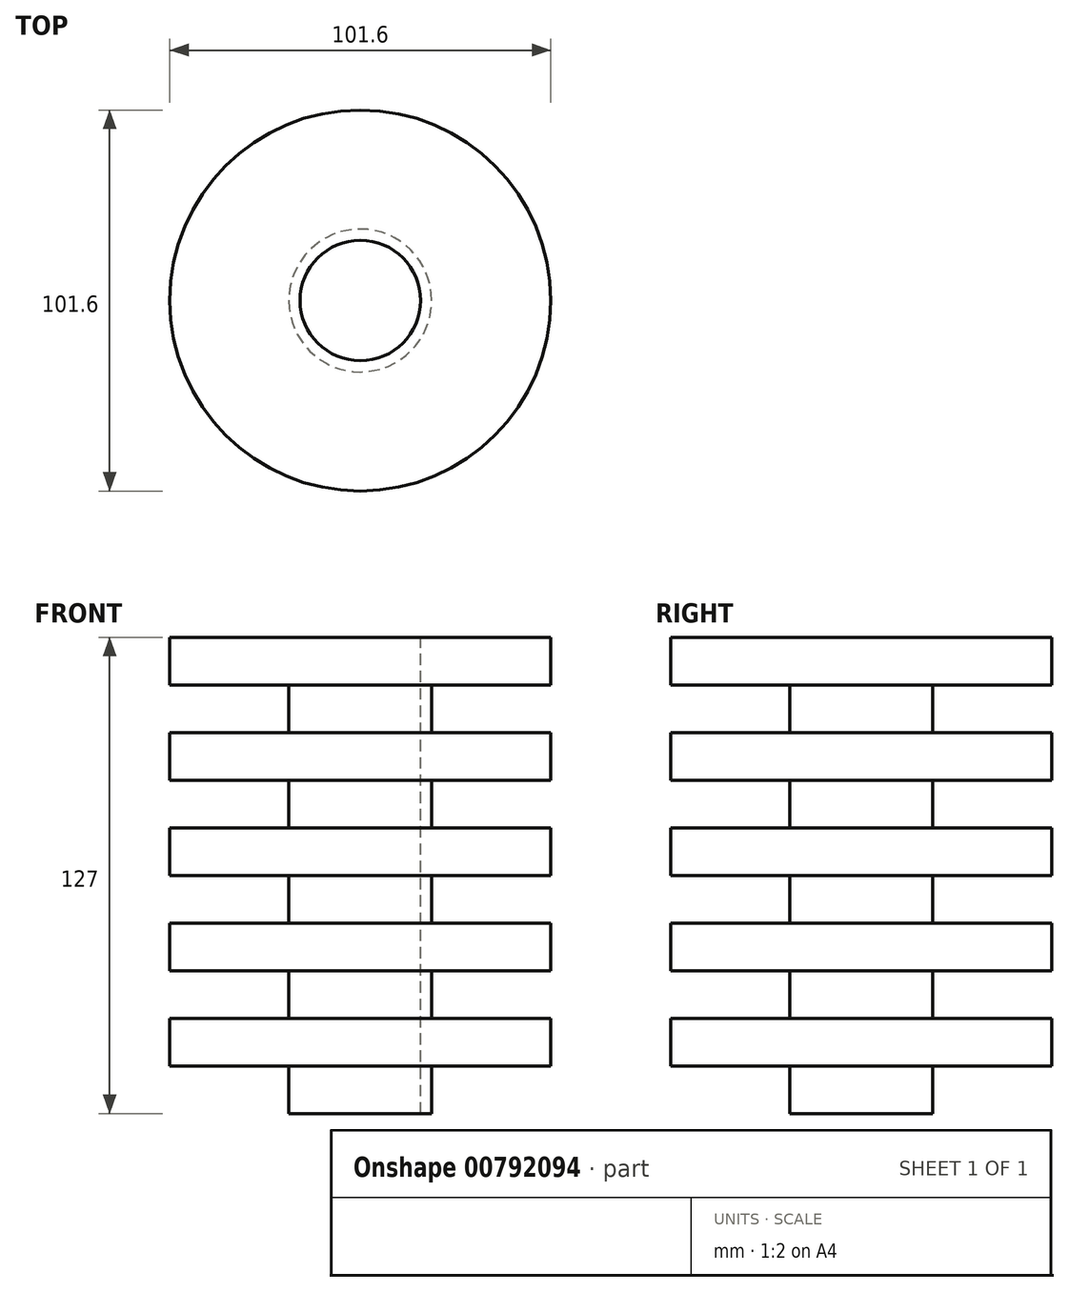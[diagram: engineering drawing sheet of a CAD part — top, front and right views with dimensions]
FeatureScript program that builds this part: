
annotation { "Feature Type Name" : "Feature", "Feature Type Description" : "" }
export const myFeature = defineFeature(function(context is Context, id is Id, definition is map)
    precondition{}
    {
        {
            var Q0;
            Q0=qCreatedBy(makeId("Front.planeOp"),FACE);
            var sketch = newSketch(context, id + "F0", { "sketchPlane" : qUnion([Q0])});
            skLineSegment(sketch, "E0", {"start": v(0, 0) * mm, "end": v(0, 127) * mm});
            skLineSegment(sketch, "E1", {"start": v(0, 127) * mm, "end": v(50.8, 127) * mm});
            skLineSegment(sketch, "E2", {"start": v(50.8, 127) * mm, "end": v(50.8, 114.3) * mm});
            skLineSegment(sketch, "E3", {"start": v(50.8, 114.3) * mm, "end": v(19.05, 114.3) * mm});
            skLineSegment(sketch, "E4", {"start": v(19.05, 114.3) * mm, "end": v(19.05, 101.6) * mm});
            skLineSegment(sketch, "E5", {"start": v(19.05, 101.6) * mm, "end": v(50.8, 101.6) * mm});
            skLineSegment(sketch, "E6", {"start": v(50.8, 101.6) * mm, "end": v(50.8, 88.9) * mm});
            skLineSegment(sketch, "E7", {"start": v(50.8, 88.9) * mm, "end": v(19.05, 88.9) * mm});
            skLineSegment(sketch, "E8", {"start": v(19.05, 88.9) * mm, "end": v(19.05, 76.2) * mm});
            skLineSegment(sketch, "E9", {"start": v(19.05, 76.2) * mm, "end": v(50.8, 76.2) * mm});
            skLineSegment(sketch, "E10", {"start": v(50.8, 76.2) * mm, "end": v(50.8, 63.5) * mm});
            skLineSegment(sketch, "E11", {"start": v(50.8, 63.5) * mm, "end": v(19.05, 63.5) * mm});
            skLineSegment(sketch, "E12", {"start": v(19.05, 63.5) * mm, "end": v(19.05, 50.8) * mm});
            skLineSegment(sketch, "E13", {"start": v(19.05, 50.8) * mm, "end": v(50.8, 50.8) * mm});
            skLineSegment(sketch, "E14", {"start": v(50.8, 50.8) * mm, "end": v(50.8, 38.1) * mm});
            skLineSegment(sketch, "E15", {"start": v(50.8, 38.1) * mm, "end": v(19.05, 38.1) * mm});
            skLineSegment(sketch, "E16", {"start": v(19.05, 38.1) * mm, "end": v(19.05, 25.4) * mm});
            skLineSegment(sketch, "E17", {"start": v(19.05, 25.4) * mm, "end": v(50.8, 25.4) * mm});
            skLineSegment(sketch, "E18", {"start": v(50.8, 25.4) * mm, "end": v(50.8, 12.7) * mm});
            skLineSegment(sketch, "E19", {"start": v(50.8, 12.7) * mm, "end": v(19.05, 12.7) * mm});
            skLineSegment(sketch, "E20", {"start": v(19.05, 12.7) * mm, "end": v(19.05, 0) * mm});
            skLineSegment(sketch, "E21", {"start": v(19.05, 0) * mm, "end": v(0, 0) * mm});
            skSolve(sketch);
        }
        {
            var Q0;
            Q0=makeQuery(id+"F0.imprint","IMPRINT",FACE,{"disambiguationData":[TD([[makeQuery(id+"F0.imprint","IMPRINT",EDGE,{"derivedFrom":sQuery(id+"F0.wireOp",EDGE,"E0")}),-1.0]])]});
            var Q1;
            Q1=sQuery(id+"F0.wireOp",EDGE,"E0");
            revolve(context, id + "F1", {"surfaceOperationType" : NewSurfaceOperationType.NEW, "entities" : qUnion([Q0]), "axis" : qUnion([Q1]), "revolveType" : RevolveType.FULL});
        }
        {
            var Q0;
            Q0=makeQuery(id+"F1.opRevolve","SWEPT_FACE",FACE,{"disambiguationData":[OSD([sQuery(id+"F0.wireOp",EDGE,"E1")])]});
            var sketch = newSketch(context, id + "F2", { "sketchPlane" : qUnion([Q0])});
            skSolve(sketch);
        }
        {
            var Q0;
            Q0=makeQuery(id+"F2.imprint","IMPRINT",FACE,{"disambiguationData":[TD([[makeQuery(id+"F2.imprint","IMPRINT",EDGE,{"derivedFrom":makeQuery(id+"F1.opRevolve","SWEPT_EDGE",EDGE,{"disambiguationData":[OSD([sQuery(id+"F0.wireOp",EDGE,"E1"),sQuery(id+"F0.wireOp",EDGE,"E2")])]})}),-1.0]])]});
            var sketch = newSketch(context, id + "F3", { "sketchPlane" : qUnion([Q0])});
            skCircle(sketch, "E22", {"center": v(0, 0) * mm, "radius": 18.28 * mm});
            skSolve(sketch);
        }
        {
            var Q0;
            Q0 = qSketchRegion(id + "F3", true);
            extrude(context, id + "F4", {"entities" : qUnion([Q0]), "operationType" : NewBodyOperationType.REMOVE, "endBound" : BoundingType.THROUGH_ALL, "depth" : 25.4 * mm, "offsetDistance" : 25.4 * mm});
        }
        {
            var Q0;
            Q0=makeQuery(id+"F2.imprint","IMPRINT",FACE,{"disambiguationData":[TD([[makeQuery(id+"F2.imprint","IMPRINT",EDGE,{"derivedFrom":makeQuery(id+"F1.opRevolve","SWEPT_EDGE",EDGE,{"disambiguationData":[OSD([sQuery(id+"F0.wireOp",EDGE,"E1"),sQuery(id+"F0.wireOp",EDGE,"E2")])]})}),-1.0]])]});
            var sketch = newSketch(context, id + "F5", { "sketchPlane" : qUnion([Q0])});
            skCircle(sketch, "E23", {"center": v(0, 0) * mm, "radius": 16.06 * mm});
            skSolve(sketch);
        }
        {
            var Q0;
            Q0 = qSketchRegion(id + "F5", true);
            extrude(context, id + "F6", {"entities" : qUnion([Q0]), "operationType" : NewBodyOperationType.REMOVE, "endBound" : BoundingType.THROUGH_ALL, "oppositeDirection" : true, "depth" : 25.4 * mm, "offsetDistance" : 25.4 * mm});
        }
    });
